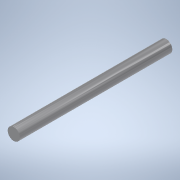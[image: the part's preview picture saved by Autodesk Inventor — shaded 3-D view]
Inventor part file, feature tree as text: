
AUTODESK INVENTOR PART (.ipt)
format: ipt  version: 2020 (Build 240168000, 168)  size: 89,600 bytes
history: native  units: mm
features: extrude x1, sketch x1
ambient origin geometry x8: Origin, YZ Plane, XZ Plane, XY Plane, X Axis, Y Axis, Z Axis, Center Point
bodies: Solid1 (feature_tree)
feature tree (2):
  extrude  "Extrusion1"  Depth=25.0mm TaperAngle=0.0deg
  sketch  "Sketch2"  dims[d0=2.0mm d1=25.0mm d2=0.0mm]
